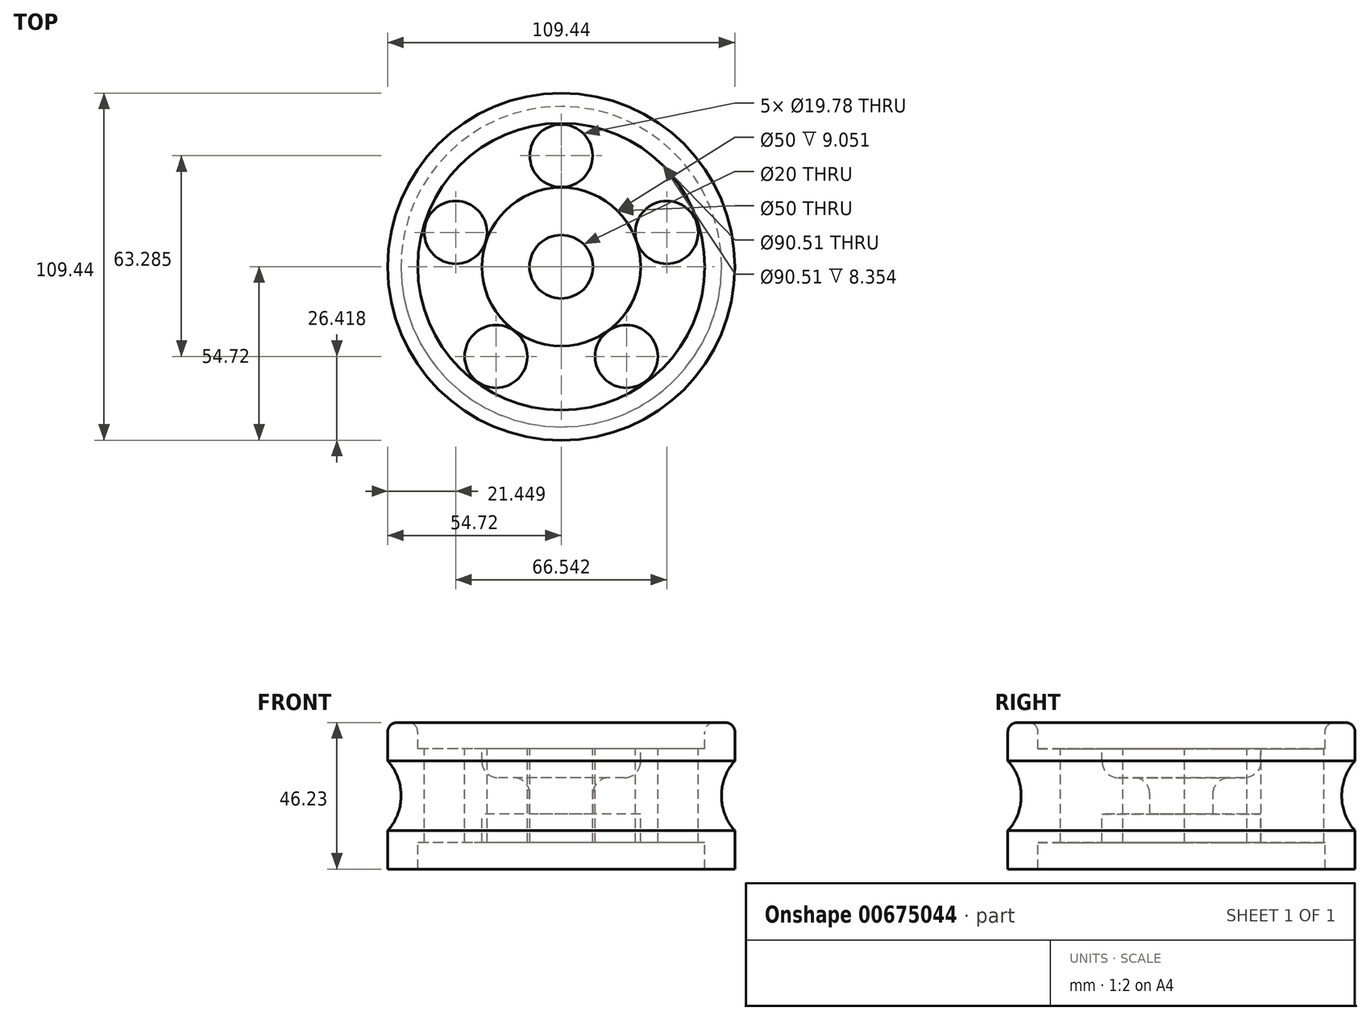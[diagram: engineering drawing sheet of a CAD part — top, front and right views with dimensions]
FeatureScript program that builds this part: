
annotation { "Feature Type Name" : "Feature", "Feature Type Description" : "" }
export const myFeature = defineFeature(function(context is Context, id is Id, definition is map)
    precondition{}
    {
        {
            var Q0;
            Q0=qCreatedBy(makeId("Front.planeOp"),FACE);
            var sketch = newSketch(context, id + "F0", { "sketchPlane" : qUnion([Q0])});
            skLineSegment(sketch, "E0", {"start": v(0, 54.3) * mm, "end": v(0, 0) * mm, "construction": true});
            skLineSegment(sketch, "E1", {"start": v(0, 23.53) * mm, "end": v(-57.65, 23.53) * mm, "construction": true});
            skPoint(sketch, "E2.orphan", {"position": v(-38.64, 23.53) * mm});
            skLineSegment(sketch, "E3", {"start": v(-10, 23.53) * mm, "end": v(-10, 29.24) * mm});
            skLineSegment(sketch, "E4", {"start": v(-10, 29.24) * mm, "end": v(-25, 29.24) * mm});
            skLineSegment(sketch, "E5", {"start": v(-25, 29.24) * mm, "end": v(-25, 38.3) * mm});
            skLineSegment(sketch, "E6", {"start": v(-25, 38.3) * mm, "end": v(-45.25, 38.3) * mm});
            skLineSegment(sketch, "E7", {"start": v(-45.25, 38.3) * mm, "end": v(-45.25, 46.65) * mm});
            skLineSegment(sketch, "E8", {"start": v(-45.25, 46.65) * mm, "end": v(-54.72, 46.65) * mm});
            skLineSegment(sketch, "E9", {"start": v(-54.72, 46.65) * mm, "end": v(-54.72, 34.53) * mm});
            skLineSegment(sketch, "E10", {"start": v(-54.72, 34.53) * mm, "end": v(-50.54, 34.53) * mm});
            skLineSegment(sketch, "E11", {"start": v(-50.54, 34.53) * mm, "end": v(-50.54, 23.53) * mm});
            skLineSegment(sketch, "E12.MirrorCS", {"start": v(-54.72, 0.42) * mm, "end": v(-54.72, 12.53) * mm});
            skLineSegment(sketch, "E13.MirrorCS", {"start": v(-25, 17.82) * mm, "end": v(-25, 8.77) * mm});
            skLineSegment(sketch, "E14.MirrorCS", {"start": v(-25, 8.77) * mm, "end": v(-45.25, 8.77) * mm});
            skLineSegment(sketch, "E15.MirrorCS", {"start": v(-10, 17.82) * mm, "end": v(-25, 17.82) * mm});
            skLineSegment(sketch, "E16.MirrorCS", {"start": v(-45.25, 0.42) * mm, "end": v(-54.72, 0.42) * mm});
            skLineSegment(sketch, "E17.MirrorCS", {"start": v(-45.25, 8.77) * mm, "end": v(-45.25, 0.42) * mm});
            skLineSegment(sketch, "E18.MirrorCS", {"start": v(-10, 23.53) * mm, "end": v(-10, 17.82) * mm});
            skLineSegment(sketch, "E19.MirrorCS", {"start": v(-54.72, 12.53) * mm, "end": v(-50.54, 12.53) * mm});
            skLineSegment(sketch, "E20.MirrorCS", {"start": v(-50.54, 12.53) * mm, "end": v(-50.54, 23.53) * mm});
            skLineSegment(sketch, "E21", {"start": v(-45.25, 0.42) * mm, "end": v(0, 0) * mm, "construction": true});
            skSolve(sketch);
        }
        {
            var Q0;
            Q0=makeQuery(id+"F0.imprint","IMPRINT",FACE,{"disambiguationData":[TD([[makeQuery(id+"F0.imprint","IMPRINT",EDGE,{"derivedFrom":sQuery(id+"F0.wireOp",EDGE,"E3")}),1.0]])]});
            var Q1;
            Q1=sQuery(id+"F0.wireOp",EDGE,"E0");
            revolve(context, id + "F1", {"entities" : qUnion([Q0]), "axis" : qUnion([Q1]), "revolveType" : RevolveType.FULL});
        }
        {
            var Q0;
            Q0=makeQuery(id+"F1.opRevolve","SWEPT_FACE",FACE,{"disambiguationData":[OSD([sQuery(id+"F0.wireOp",EDGE,"E11"),sQuery(id+"F0.wireOp",EDGE,"E20.MirrorCS")])]});
            fillet(context, id + "F2", {"entities" : qUnion([Q0]), "radius" : 16 * mm, "tangentPropagation" : true, "allowEdgeOverflow" : false});
        }
        {
            var Q0;
            Q0=makeQuery(id+"F1.opRevolve","SWEPT_FACE",FACE,{"disambiguationData":[OSD([sQuery(id+"F0.wireOp",EDGE,"E6")])]});
            var sketch = newSketch(context, id + "F3", { "sketchPlane" : qUnion([Q0])});
            skCircle(sketch, "E22", {"center": v(0, 0) * mm, "radius": 25.04 * mm, "construction": true});
            skCircle(sketch, "E23", {"center": v(0, 0) * mm, "radius": 44.93 * mm, "construction": true});
            skLineSegment(sketch, "E24", {"start": v(0, 25.04) * mm, "end": v(0, 44.93) * mm, "construction": true});
            skCircle(sketch, "E25", {"center": v(0, 34.98) * mm, "radius": 9.9 * mm});
            skCircle(sketch, "E26.1.0", {"center": v(-33.27, 10.81) * mm, "radius": 9.9 * mm});
            skCircle(sketch, "E26.2.0", {"center": v(-20.56, -28.3) * mm, "radius": 9.9 * mm});
            skCircle(sketch, "E26.3.0", {"center": v(20.56, -28.3) * mm, "radius": 9.9 * mm});
            skCircle(sketch, "E26.4.0", {"center": v(33.27, 10.81) * mm, "radius": 9.9 * mm});
            skSolve(sketch);
        }
        {
            var Q0;
            Q0=makeQuery(id+"F3.imprint","IMPRINT",FACE,{"disambiguationData":[TD([[makeQuery(id+"F3.imprint","IMPRINT",EDGE,{"derivedFrom":sQuery(id+"F3.wireOp",EDGE,"E25")}),1.0]])]});
            var Q1;
            Q1=makeQuery(id+"F3.imprint","IMPRINT",FACE,{"disambiguationData":[TD([[makeQuery(id+"F3.imprint","IMPRINT",EDGE,{"derivedFrom":sQuery(id+"F3.wireOp",EDGE,"E26.4.0")}),1.0]])]});
            var Q2;
            Q2=makeQuery(id+"F3.imprint","IMPRINT",FACE,{"disambiguationData":[TD([[makeQuery(id+"F3.imprint","IMPRINT",EDGE,{"derivedFrom":sQuery(id+"F3.wireOp",EDGE,"E26.3.0")}),1.0]])]});
            var Q3;
            Q3=makeQuery(id+"F3.imprint","IMPRINT",FACE,{"disambiguationData":[TD([[makeQuery(id+"F3.imprint","IMPRINT",EDGE,{"derivedFrom":sQuery(id+"F3.wireOp",EDGE,"E26.2.0")}),1.0]])]});
            var Q4;
            Q4=makeQuery(id+"F3.imprint","IMPRINT",FACE,{"disambiguationData":[TD([[makeQuery(id+"F3.imprint","IMPRINT",EDGE,{"derivedFrom":sQuery(id+"F3.wireOp",EDGE,"E26.1.0")}),1.0]])]});
            extrude(context, id + "F4", {"entities" : qUnion([Q0, Q1, Q2, Q3, Q4]), "operationType" : NewBodyOperationType.REMOVE, "oppositeDirection" : true, "depth" : 50 * mm, "offsetDistance" : 25 * mm});
        }
        {
            var Q0;
            Q0=makeQuery(id+"F1.opRevolve","SWEPT_FACE",FACE,{"disambiguationData":[OSD([sQuery(id+"F0.wireOp",EDGE,"E6")])]});
            fillet(context, id + "F5", {"entities" : qUnion([Q0]), "radius" : 0.02 * mm, "tangentPropagation" : true, "allowEdgeOverflow" : false});
        }
        {
            var Q0;
            Q0=makeQuery(id+"F1.opRevolve","SWEPT_FACE",FACE,{"disambiguationData":[OSD([sQuery(id+"F0.wireOp",EDGE,"E8")])]});
            fillet(context, id + "F6", {"entities" : qUnion([Q0]), "radius" : 3 * mm, "tangentPropagation" : true, "allowEdgeOverflow" : false});
        }
        {
            var Q0;
            Q0=makeQuery(id+"F1.opRevolve","SWEPT_FACE",FACE,{"disambiguationData":[OSD([sQuery(id+"F0.wireOp",EDGE,"E4")])]});
            fillet(context, id + "F7", {"entities" : qUnion([Q0]), "radius" : 5 * mm, "tangentPropagation" : true, "allowEdgeOverflow" : false});
        }
    });
